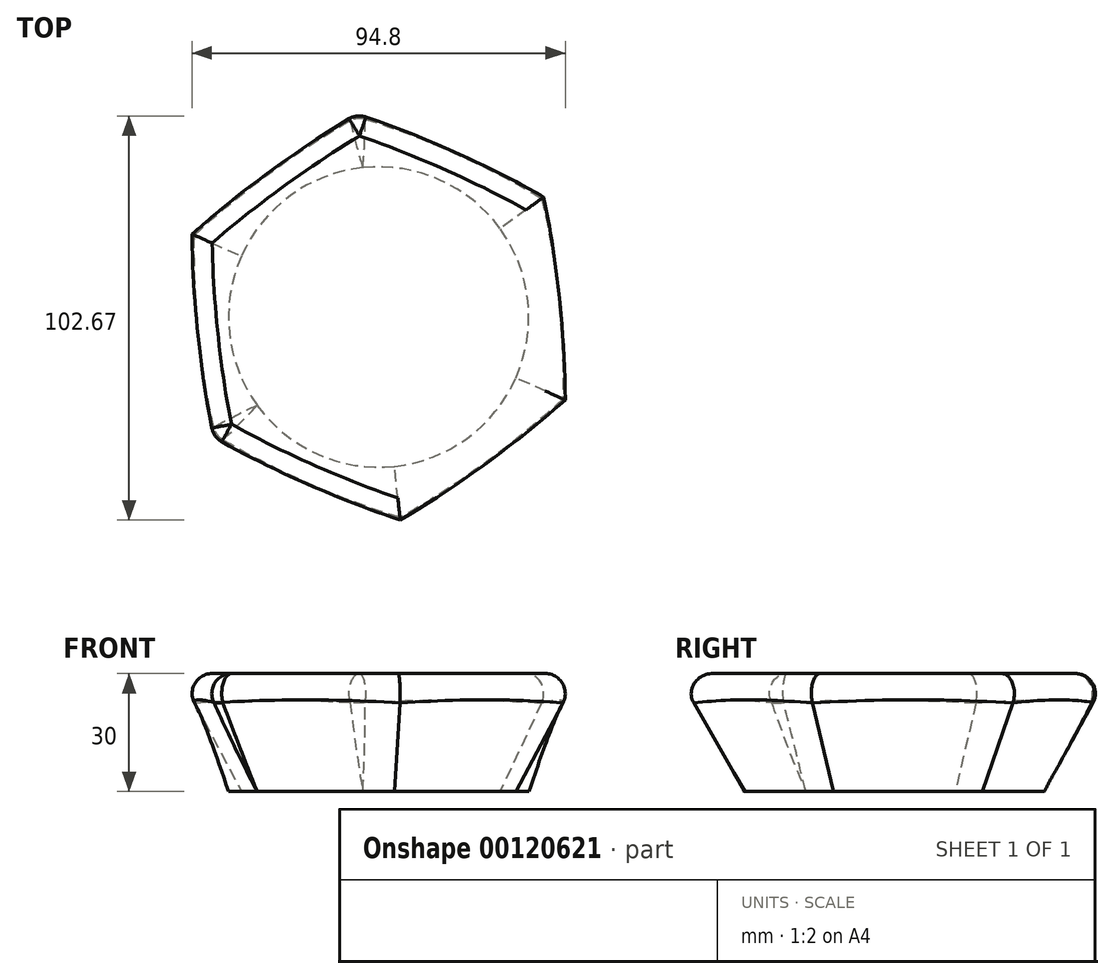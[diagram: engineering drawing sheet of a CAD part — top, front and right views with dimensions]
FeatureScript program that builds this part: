
annotation { "Feature Type Name" : "Feature", "Feature Type Description" : "" }
export const myFeature = defineFeature(function(context is Context, id is Id, definition is map)
    precondition{}
    {
        {
            var Q0;
            Q0=qCreatedBy(makeId("Top.planeOp"),FACE);
            var sketch = newSketch(context, id + "F0", { "sketchPlane" : qUnion([Q0])});
            skCircle(sketch, "E0", {"center": v(0, 0) * mm, "radius": 38.14 * mm});
            skSolve(sketch);
        }
        {
            var Q0;
            Q0=qCreatedBy(makeId("Top.planeOp"),FACE);
            cPlane(context, id + "F1", {"entities" : qUnion([Q0]), "cplaneType" : CPlaneType.OFFSET, "offset" : 30 * mm, "width" : 152.4 * mm, "height" : 152.4 * mm});
        }
        {
            var Q0;
            Q0=qCreatedBy(id+"F1.planeOp",FACE);
            var sketch = newSketch(context, id + "F2", { "sketchPlane" : qUnion([Q0])});
            skCircle(sketch, "E1.cCircle", {"center": v(0, 0) * mm, "radius": 48.1 * mm, "construction": true});
            skLineSegment(sketch, "E1.0", {"start": v(50.76, -22.54) * mm, "end": v(5.86, -55.23) * mm});
            skLineSegment(sketch, "E1.1", {"start": v(5.86, -55.23) * mm, "end": v(-44.9, -32.69) * mm});
            skLineSegment(sketch, "E1.2", {"start": v(-44.9, -32.69) * mm, "end": v(-50.76, 22.54) * mm});
            skLineSegment(sketch, "E1.3", {"start": v(-50.76, 22.54) * mm, "end": v(-5.86, 55.23) * mm});
            skLineSegment(sketch, "E1.4", {"start": v(-5.86, 55.23) * mm, "end": v(44.9, 32.69) * mm});
            skLineSegment(sketch, "E1.5", {"start": v(44.9, 32.69) * mm, "end": v(50.76, -22.54) * mm});
            skPoint(sketch, "E1.0.midPoint", {"position": v(28.3, -38.89) * mm});
            skSolve(sketch);
        }
        {
            var Q0;
            Q0=makeQuery(id+"F2.imprint","IMPRINT",FACE,{"disambiguationData":[TD([[makeQuery(id+"F2.imprint","IMPRINT",EDGE,{"derivedFrom":sQuery(id+"F2.wireOp",EDGE,"E1.0")}),-1.0]])]});
            var Q1;
            Q1=makeQuery(id+"F0.imprint","IMPRINT",FACE,{"disambiguationData":[TD([[makeQuery(id+"F0.imprint","IMPRINT",EDGE,{"derivedFrom":sQuery(id+"F0.wireOp",EDGE,"E0")}),1.0]])]});
            loft(context, id + "F3", {"sheetProfilesArray" : [{ "sheetProfileEntities" : qUnion([Q0]) }, { "sheetProfileEntities" : qUnion([Q1]) }]});
        }
        {
            var Q0;
            Q0=makeQuery(id+"F3.opLoft","MID_CAP_EDGE",EDGE,{"disambiguationData":[OSD([sQuery(id+"F2.wireOp",EDGE,"E1.1"),sQuery(id+"F2.wireOp",EDGE,"E1.2"),sQuery(id+"F2.wireOp",EDGE,"E1.3")])],"capPos":0.0});
            var Q1;
            Q1=makeQuery(id+"F3.opLoft","MID_CAP_EDGE",EDGE,{"disambiguationData":[OSD([sQuery(id+"F2.wireOp",EDGE,"E1.2"),sQuery(id+"F2.wireOp",EDGE,"E1.3"),sQuery(id+"F2.wireOp",EDGE,"E1.4")])],"capPos":0.0});
            fillet(context, id + "F4", {"entities" : qUnion([Q0, Q1]), "radius" : 5.08 * mm, "tangentPropagation" : true, "allowEdgeOverflow" : false});
        }
        {
            var Q0;
            Q0=makeQuery(id+"F3.opLoft","MID_CAP_EDGE",EDGE,{"disambiguationData":[OSD([sQuery(id+"F2.wireOp",EDGE,"E1.3"),sQuery(id+"F2.wireOp",EDGE,"E1.4"),sQuery(id+"F2.wireOp",EDGE,"E1.5")])],"capPos":0.0});
            var Q1;
            Q1=makeQuery(id+"F3.opLoft","MID_CAP_EDGE",EDGE,{"disambiguationData":[OSD([sQuery(id+"F2.wireOp",EDGE,"E1.0"),sQuery(id+"F2.wireOp",EDGE,"E1.4"),sQuery(id+"F2.wireOp",EDGE,"E1.5")])],"capPos":0.0});
            var Q2;
            Q2=makeQuery(id+"F3.opLoft","MID_CAP_EDGE",EDGE,{"disambiguationData":[OSD([sQuery(id+"F2.wireOp",EDGE,"E1.0"),sQuery(id+"F2.wireOp",EDGE,"E1.1"),sQuery(id+"F2.wireOp",EDGE,"E1.5")])],"capPos":0.0});
            var Q3;
            Q3=makeQuery(id+"F3.opLoft","MID_CAP_EDGE",EDGE,{"disambiguationData":[OSD([sQuery(id+"F2.wireOp",EDGE,"E1.0"),sQuery(id+"F2.wireOp",EDGE,"E1.1"),sQuery(id+"F2.wireOp",EDGE,"E1.2")])],"capPos":0.0});
            fillet(context, id + "F5", {"entities" : qUnion([Q0, Q1, Q2, Q3]), "radius" : 5.08 * mm, "tangentPropagation" : true, "allowEdgeOverflow" : false});
        }
    });
